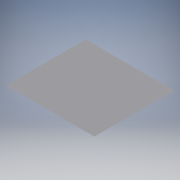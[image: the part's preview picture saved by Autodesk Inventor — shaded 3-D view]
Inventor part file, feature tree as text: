
AUTODESK INVENTOR PART (.ipt)
format: ipt  version: 2018 (Build 220112000, 112)  size: 98,816 bytes
history: native  units: mm
features: extrude x1, chamfer x1, sketch x1
ambient origin geometry x8: Origin, YZ Plane, XZ Plane, XY Plane, X Axis, Y Axis, Z Axis, Center Point
bodies: Volumenkörper1 (feature_tree)
feature tree (3):
  extrude  "Extrusion1"  Depth=20.0mm
  chamfer  "Fase1"  Distance=20.0mm
  sketch  "Skizze1"  dims[d0=500.0mm d1=450.0mm d2=20.0mm d3=0.0mm d4=20.0mm d5=2.0mm d6=45.0deg]
